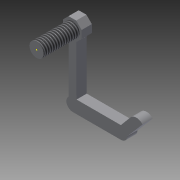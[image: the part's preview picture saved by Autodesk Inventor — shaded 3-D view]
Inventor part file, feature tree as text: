
AUTODESK INVENTOR PART (.ipt)
format: ipt  version: 2015 SP2 (Build 190223200, 223)  size: 137,216 bytes
history: native  units: mm
features: sketch x15, extrude x8, thread x1
ambient origin geometry x8: Origin, YZ Plane, XZ Plane, XY Plane, X Axis, Y Axis, Z Axis, Center Point
bodies: Solid1 (feature_tree)
feature tree (24):
  sketch  "Sketch1"  dims[d0=2.8mm d1=7.0mm d2=0.0mm]
  sketch  "Sketch2"  dims[d4=2.0mm d5=0.0mm d6=10.0mm d7=0.0mm]
  extrude  "Extrusion1"  Depth=7.0mm TaperAngle=0.0deg
  extrude  "Extrusion2"  Depth=10.0mm TaperAngle=0.0deg
  extrude  "Extrusion3"  Depth=2.0mm TaperAngle=0.0deg
  sketch  "Sketch5"  dims[d18=2.0mm d19=0.0mm d20=8.726646mm]
  sketch  "Sketch6"  dims[d21=2.0mm d22=0.0mm]
  thread  "Thread1"  [1 undecoded]
  extrude  "Extrusion4"  Depth=2.0mm
  sketch  "Sketch8"
  sketch  "Sketch9"
  extrude  "Extrusion5"  Depth=2.0mm
  sketch  "Sketch11"
  sketch  "Sketch12"
  extrude  "Extrusion6"  [1 undecoded]
  extrude  "Extrusion7"  [1 undecoded]
  extrude  "Extrusion8"  [1 undecoded]
  sketch  "Sketch3"  dims[d8=10.0mm d9=0.0mm d10=2.0mm d11=0.0mm d12=4.0mm d13=0.0mm]
  sketch  "Sketch4"  dims[d15=2.0mm d16=0.0mm d17=2.483mm]
  sketch  "Sketch7"
  sketch  "Sketch10"
  sketch  "Sketch13"
  sketch  "Sketch14"
  sketch  "Sketch15"
note: 4 required parameter values undecoded (feature->parameter linkage not recoverable at this tier; creation-order binding heuristic only, values carry confidence <= 0.55)
